# Revit family: AM2 TOP PORTS
name_source: partatom
category: Mechanical Equipment
units: mm (PartAtom-declared; Revit-internal decimal feet)

## family parameters
Always vertical = Yes
Classification = None
Cut with Voids When Loaded = No
Maintain Annotation Orientation = No
OmniClass Number = 23.75.70.00
OmniClass Title = HVAC Distribution Devices
Part Type = Normal
Room Calculation Point = No
Round Connector Dimension = Use Diameter
Shared = No
Work Plane-Based = No

## types (1)
- Standard
    Connector_1_Diameter = 0' - 5 15/16"
    Connector_2_Diameter = 0' - 5 15/16"
    Connector_3_Diameter = 0' - 5 15/16"
    Connector_4_Diameter = 0' - 5 15/16"
    Default Elevation = 0' - 0"
    Description = AM2 TANDEMS
    Design State = 1
    Manufacturer = Broan Nutone Venmar
    Model = AM2 TANDEMS
    Part Number = AM2 TOP PORTS
    Preprocessor = CREO PARAMETRIC BY PTC INC, 2020414
    Revision Number = 1LAST_VERSION
    Sending System = CREO PARAMETRIC BY PTC INC, 2020414
    Title = 3D_AIR_MASTER_2

## geometry (parser evidence)
native form markers: Sweep x3
no freeform markers — native parametric forms only
